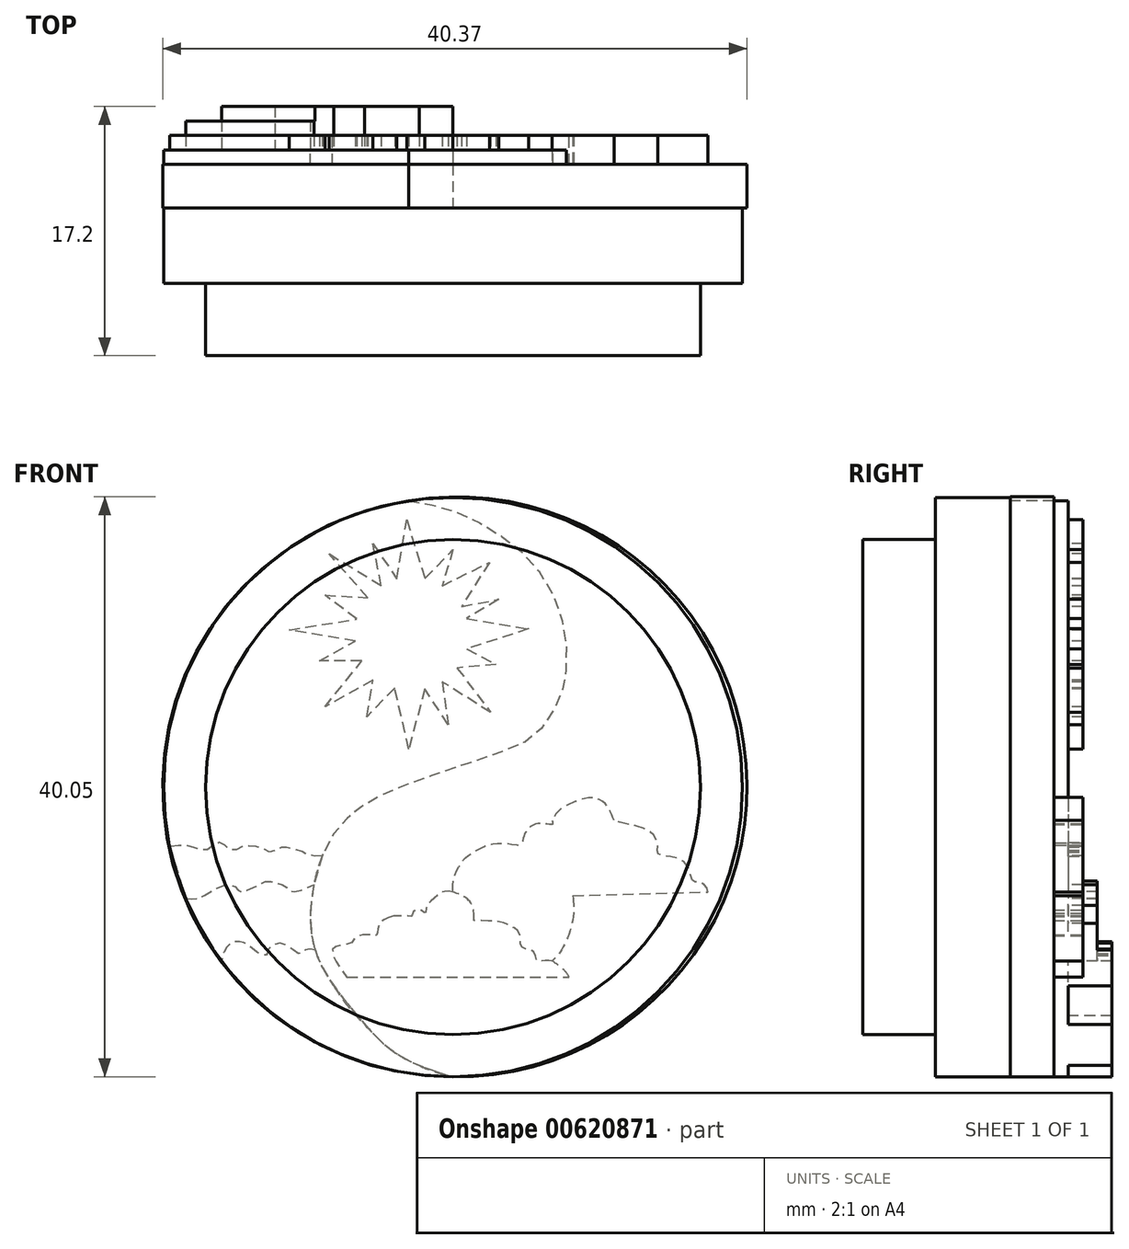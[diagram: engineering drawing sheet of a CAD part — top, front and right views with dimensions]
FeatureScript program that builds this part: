
annotation { "Feature Type Name" : "Feature", "Feature Type Description" : "" }
export const myFeature = defineFeature(function(context is Context, id is Id, definition is map)
    precondition{}
    {
        {
            var Q0;
            Q0=qCreatedBy(makeId("Front.planeOp"),FACE);
            var sketch = newSketch(context, id + "F0", { "sketchPlane" : qUnion([Q0])});
            skCircle(sketch, "E0", {"center": v(0, 0) * mm, "radius": 20 * mm});
            skSolve(sketch);
        }
        {
            var Q0;
            Q0=makeQuery(id+"F0.imprint","IMPRINT",FACE,{"disambiguationData":[TD([[makeQuery(id+"F0.imprint","IMPRINT",EDGE,{"derivedFrom":sQuery(id+"F0.wireOp",EDGE,"E0")}),1.0]])]});
            extrude(context, id + "F1", {"entities" : qUnion([Q0]), "depth" : 5.2 * mm, "offsetDistance" : 25 * mm});
        }
        {
            var Q0;
            Q0=makeQuery(id+"F1.opExtrude","CAP_FACE",FACE,{"disambiguationData":[OSD([sQuery(id+"F0.wireOp",EDGE,"E0")])],"isStart":false});
            var sketch = newSketch(context, id + "F2", { "sketchPlane" : qUnion([Q0])});
            skCircle(sketch, "E1", {"center": v(0, 0) * mm, "radius": 17.1 * mm});
            skSolve(sketch);
        }
        {
            var Q0;
            Q0 = qSketchRegion(id + "F2", true);
            extrude(context, id + "F3", {"entities" : qUnion([Q0]), "operationType" : NewBodyOperationType.ADD, "depth" : 5 * mm, "offsetDistance" : 25 * mm});
        }
        {
            var Q0;
            Q0=makeQuery(id+"F1.opExtrude","CAP_FACE",FACE,{"disambiguationData":[OSD([sQuery(id+"F0.wireOp",EDGE,"E0")])],"isStart":true});
            var sketch = newSketch(context, id + "F4", { "sketchPlane" : qUnion([Q0])});
            skFitSpline(sketch, "E2", {"points": [v(3.07, 19.76) * mm, v(0, 19.09) * mm, v(-3.3, 17.36) * mm, v(-5.79, 15.1) * mm, v(-7.57, 11.43) * mm, v(-7.8, 8.17) * mm, v(-7.39, 6.2) * mm, v(-5.84, 3.77) * mm, v(-3.11, 2.35) * mm, v(3.65, 0) * mm, v(5.9, -1.1) * mm, v(7.45, -2.28) * mm, v(8.87, -4.36) * mm, v(9.7, -7.26) * mm, v(9.76, -10.23) * mm, v(8.81, -12.84) * mm, v(6.8, -15.57) * mm, v(3.89, -18.42) * mm, v(0, -20) * mm], "startDerivative": vector(-55.85, -8.29) * mm, "endDerivative": vector(-65.14, -19.54) * mm});
            skArc(sketch, "E3", {"start": v(3.07, 19.76) * mm, "mid": v(-20.25, 1.56) * mm, "end": v(0, -20) * mm});
            skArc(sketch, "E4", {"start": v(0, -20) * mm, "mid": v(20, -1.54) * mm, "end": v(3.07, 19.76) * mm});
            skFitSpline(sketch, "E5", {"points": [v(9, -4.63) * mm, v(10.3, -4.6) * mm, v(11.5, -4.13) * mm, v(12.14, -4.1) * mm, v(12.34, -4.58) * mm, v(12.1, -5) * mm, v(11.42, -4.83) * mm], "startDerivative": vector(6.16, -0.53) * mm, "endDerivative": vector(-4.8, 2.3) * mm});
            skFitSpline(sketch, "E6", {"points": [v(12.34, -4.5) * mm, v(12.92, -4.39) * mm, v(13.68, -4.12) * mm, v(14.24, -3.86) * mm, v(14.85, -4.03) * mm, v(14.7, -4.75) * mm, v(14.24, -5.02) * mm, v(13.87, -4.83) * mm, v(13.87, -4.58) * mm], "startDerivative": vector(4.3, 0.69) * mm, "endDerivative": vector(0.78, 3.1) * mm});
            skSolve(sketch);
        }
        {
            var Q0;
            {var subQ0=sQuery(id+"F4.wireOp",EDGE,"E2");Q0=makeQuery(id+"F4.imprint","IMPRINT",FACE,{"disambiguationData":[TD([[makeQuery(id+"F4.imprint","IMPRINT",EDGE,{"derivedFrom":subQ0}),1.0]])]});}
            extrude(context, id + "F5", {"entities" : qUnion([Q0]), "operationType" : NewBodyOperationType.ADD, "depth" : 4 * mm, "offsetDistance" : 25 * mm});
        }
        {
            var Q0;
            Q0 = qSketchRegion(id + "F4", true);
            var Q1;
            Q1=makeQuery(id+"F1.opExtrude","CAP_FACE",FACE,{"disambiguationData":[OSD([sQuery(id+"F0.wireOp",EDGE,"E0")])],"isStart":true});
            extrude(context, id + "F6", {"entities" : qUnion([Q0, Q1]), "operationType" : NewBodyOperationType.ADD, "depth" : 3 * mm, "offsetDistance" : 25 * mm});
        }
        {
            var Q0;
            Q0=makeQuery(id+"F5.opExtrude","CAP_FACE",FACE,{"disambiguationData":[OSD([sQuery(id+"F0.wireOp",EDGE,"E0"),sQuery(id+"F4.wireOp",EDGE,"E2")])],"isStart":false});
            var sketch = newSketch(context, id + "F7", { "sketchPlane" : qUnion([Q0])});
            skCircle(sketch, "E7", {"center": v(2.85, 10.6) * mm, "radius": 3.93 * mm});
            skPoint(sketch, "E7.first.point", {"position": v(3.06, 14.51) * mm});
            skPoint(sketch, "E7.second.point", {"position": v(2.98, 6.67) * mm});
            skPoint(sketch, "E7.third.point", {"position": v(4.45, 7) * mm});
            skLineSegment(sketch, "E8", {"start": v(1.94, 6.77) * mm, "end": v(3.06, 2.64) * mm});
            skLineSegment(sketch, "E9", {"start": v(3.06, 2.64) * mm, "end": v(4.03, 6.84) * mm});
            skLineSegment(sketch, "E10", {"start": v(4.03, 6.84) * mm, "end": v(5.96, 4.86) * mm});
            skLineSegment(sketch, "E11", {"start": v(5.96, 4.86) * mm, "end": v(5.54, 7.38) * mm});
            skLineSegment(sketch, "E12", {"start": v(5.54, 7.38) * mm, "end": v(8.85, 5.53) * mm});
            skLineSegment(sketch, "E13", {"start": v(8.85, 5.53) * mm, "end": v(6.3, 8.71) * mm});
            skLineSegment(sketch, "E14", {"start": v(6.3, 8.71) * mm, "end": v(9.23, 8.71) * mm});
            skLineSegment(sketch, "E15", {"start": v(9.23, 8.71) * mm, "end": v(6.75, 10.08) * mm});
            skLineSegment(sketch, "E16", {"start": v(6.75, 10.08) * mm, "end": v(11.33, 10.84) * mm});
            skLineSegment(sketch, "E17", {"start": v(11.33, 10.84) * mm, "end": v(6.65, 11.61) * mm});
            skLineSegment(sketch, "E18", {"start": v(6.65, 11.61) * mm, "end": v(8.85, 13.26) * mm});
            skLineSegment(sketch, "E19", {"start": v(8.85, 13.26) * mm, "end": v(5.9, 13.08) * mm});
            skLineSegment(sketch, "E20", {"start": v(5.9, 13.08) * mm, "end": v(8.56, 16.1) * mm});
            skLineSegment(sketch, "E21", {"start": v(8.56, 16.1) * mm, "end": v(4.95, 13.91) * mm});
            skLineSegment(sketch, "E22", {"start": v(4.95, 13.91) * mm, "end": v(5.54, 16.82) * mm});
            skLineSegment(sketch, "E23", {"start": v(5.54, 16.82) * mm, "end": v(3.88, 14.38) * mm});
            skLineSegment(sketch, "E24", {"start": v(3.88, 14.38) * mm, "end": v(3.2, 18.47) * mm});
            skLineSegment(sketch, "E25", {"start": v(3.2, 18.47) * mm, "end": v(1.95, 14.41) * mm});
            skLineSegment(sketch, "E26", {"start": v(1.95, 14.41) * mm, "end": v(0, 16.4) * mm});
            skLineSegment(sketch, "E27", {"start": v(0, 16.4) * mm, "end": v(0.75, 13.91) * mm});
            skLineSegment(sketch, "E28", {"start": v(0.75, 13.91) * mm, "end": v(-2.52, 15.52) * mm});
            skLineSegment(sketch, "E29", {"start": v(-2.52, 15.52) * mm, "end": v(-0.6, 12.48) * mm});
            skLineSegment(sketch, "E30", {"start": v(-0.6, 12.48) * mm, "end": v(-3.15, 12.96) * mm});
            skLineSegment(sketch, "E31", {"start": v(-3.15, 12.96) * mm, "end": v(-0.93, 11.64) * mm});
            skLineSegment(sketch, "E32", {"start": v(-0.93, 11.64) * mm, "end": v(-5.2, 10.93) * mm});
            skLineSegment(sketch, "E33", {"start": v(-5.2, 10.93) * mm, "end": v(-0.93, 9.54) * mm});
            skLineSegment(sketch, "E34", {"start": v(-0.93, 9.54) * mm, "end": v(-2.98, 8.47) * mm});
            skLineSegment(sketch, "E35", {"start": v(-2.98, 8.47) * mm, "end": v(-0.28, 8.23) * mm});
            skLineSegment(sketch, "E36", {"start": v(-0.28, 8.23) * mm, "end": v(-2.6, 5.16) * mm});
            skLineSegment(sketch, "E37", {"start": v(-2.6, 5.16) * mm, "end": v(0.75, 7.27) * mm});
            skLineSegment(sketch, "E38", {"start": v(0.75, 7.27) * mm, "end": v(0.33, 4.32) * mm});
            skLineSegment(sketch, "E39", {"start": v(0.33, 4.32) * mm, "end": v(1.94, 6.77) * mm});
            skSolve(sketch);
        }
        {
            var Q0;
            {var subQ0=sQuery(id+"F7.wireOp",EDGE,"E7");var subQ8=makeQuery(id+"F7.imprint","INTERSECT",VERTEX,{"derivedFrom":[subQ0,sQuery(id+"F7.wireOp",EDGE,"E17"),sQuery(id+"F7.wireOp",EDGE,"E18")]});Q0=makeQuery(id+"F7.imprint","IMPRINT",FACE,{"disambiguationData":[TD([[makeQuery(id+"F7.imprint","IMPRINT",EDGE,{"disambiguationData":[TD([[subQ8,-1.0]])],"derivedFrom":subQ0}),1.0]])]});}
            var Q1;
            {var subQ0=sQuery(id+"F7.wireOp",EDGE,"E24");Q1=makeQuery(id+"F7.imprint","IMPRINT",FACE,{"disambiguationData":[TD([[makeQuery(id+"F7.imprint","IMPRINT",EDGE,{"derivedFrom":subQ0}),1.0]])]});}
            var Q2;
            {var subQ0=sQuery(id+"F7.wireOp",EDGE,"E22");Q2=makeQuery(id+"F7.imprint","IMPRINT",FACE,{"disambiguationData":[TD([[makeQuery(id+"F7.imprint","IMPRINT",EDGE,{"derivedFrom":subQ0}),1.0]])]});}
            var Q3;
            {var subQ0=sQuery(id+"F7.wireOp",EDGE,"E20");Q3=makeQuery(id+"F7.imprint","IMPRINT",FACE,{"disambiguationData":[TD([[makeQuery(id+"F7.imprint","IMPRINT",EDGE,{"derivedFrom":subQ0}),1.0]])]});}
            var Q4;
            {var subQ0=sQuery(id+"F7.wireOp",EDGE,"E18");Q4=makeQuery(id+"F7.imprint","IMPRINT",FACE,{"disambiguationData":[TD([[makeQuery(id+"F7.imprint","IMPRINT",EDGE,{"derivedFrom":subQ0}),1.0]])]});}
            var Q5;
            {var subQ0=sQuery(id+"F7.wireOp",EDGE,"E16");Q5=makeQuery(id+"F7.imprint","IMPRINT",FACE,{"disambiguationData":[TD([[makeQuery(id+"F7.imprint","IMPRINT",EDGE,{"derivedFrom":subQ0}),1.0]])]});}
            var Q6;
            {var subQ0=sQuery(id+"F7.wireOp",EDGE,"E14");Q6=makeQuery(id+"F7.imprint","IMPRINT",FACE,{"disambiguationData":[TD([[makeQuery(id+"F7.imprint","IMPRINT",EDGE,{"derivedFrom":subQ0}),1.0]])]});}
            var Q7;
            {var subQ0=sQuery(id+"F7.wireOp",EDGE,"E8");Q7=makeQuery(id+"F7.imprint","IMPRINT",FACE,{"disambiguationData":[TD([[makeQuery(id+"F7.imprint","IMPRINT",EDGE,{"derivedFrom":subQ0}),1.0]])]});}
            var Q8;
            {var subQ2=sQuery(id+"F7.wireOp",EDGE,"E38");Q8=makeQuery(id+"F7.imprint","IMPRINT",FACE,{"disambiguationData":[TD([[makeQuery(id+"F7.imprint","IMPRINT",EDGE,{"derivedFrom":subQ2}),1.0]])]});}
            var Q9;
            {var subQ0=sQuery(id+"F7.wireOp",EDGE,"E10");Q9=makeQuery(id+"F7.imprint","IMPRINT",FACE,{"disambiguationData":[TD([[makeQuery(id+"F7.imprint","IMPRINT",EDGE,{"derivedFrom":subQ0}),1.0]])]});}
            var Q10;
            {var subQ0=sQuery(id+"F7.wireOp",EDGE,"E28");Q10=makeQuery(id+"F7.imprint","IMPRINT",FACE,{"disambiguationData":[TD([[makeQuery(id+"F7.imprint","IMPRINT",EDGE,{"derivedFrom":subQ0}),1.0]])]});}
            var Q11;
            {var subQ0=sQuery(id+"F7.wireOp",EDGE,"E36");Q11=makeQuery(id+"F7.imprint","IMPRINT",FACE,{"disambiguationData":[TD([[makeQuery(id+"F7.imprint","IMPRINT",EDGE,{"derivedFrom":subQ0}),1.0]])]});}
            var Q12;
            {var subQ0=sQuery(id+"F7.wireOp",EDGE,"E34");Q12=makeQuery(id+"F7.imprint","IMPRINT",FACE,{"disambiguationData":[TD([[makeQuery(id+"F7.imprint","IMPRINT",EDGE,{"derivedFrom":subQ0}),1.0]])]});}
            var Q13;
            {var subQ0=sQuery(id+"F7.wireOp",EDGE,"E32");Q13=makeQuery(id+"F7.imprint","IMPRINT",FACE,{"disambiguationData":[TD([[makeQuery(id+"F7.imprint","IMPRINT",EDGE,{"derivedFrom":subQ0}),1.0]])]});}
            var Q14;
            {var subQ0=sQuery(id+"F7.wireOp",EDGE,"E30");Q14=makeQuery(id+"F7.imprint","IMPRINT",FACE,{"disambiguationData":[TD([[makeQuery(id+"F7.imprint","IMPRINT",EDGE,{"derivedFrom":subQ0}),1.0]])]});}
            var Q15;
            {var subQ0=sQuery(id+"F7.wireOp",EDGE,"E26");Q15=makeQuery(id+"F7.imprint","IMPRINT",FACE,{"disambiguationData":[TD([[makeQuery(id+"F7.imprint","IMPRINT",EDGE,{"derivedFrom":subQ0}),1.0]])]});}
            extrude(context, id + "F8", {"entities" : qUnion([Q0, Q1, Q2, Q3, Q4, Q5, Q6, Q7, Q8, Q9, Q10, Q11, Q12, Q13, Q14, Q15]), "operationType" : NewBodyOperationType.ADD, "depth" : 1 * mm, "offsetDistance" : 25 * mm});
        }
        {
            var Q0;
            Q0=makeQuery(id+"F5.opExtrude","CAP_FACE",FACE,{"disambiguationData":[OSD([sQuery(id+"F0.wireOp",EDGE,"E0"),sQuery(id+"F4.wireOp",EDGE,"E2")])],"isStart":false});
            var sketch = newSketch(context, id + "F9", { "sketchPlane" : qUnion([Q0])});
            skFitSpline(sketch, "E40", {"points": [v(9.04, -4.74) * mm, v(9.61, -6.74) * mm], "startDerivative": vector(0.57, -2) * mm, "endDerivative": vector(0.57, -2) * mm});
            skFitSpline(sketch, "E41", {"points": [v(9.04, -4.74) * mm, v(9.8, -4.74) * mm, v(10.5, -4.44) * mm, v(11.48, -4.16) * mm, v(11.9, -4.19) * mm, v(12.53, -4.49) * mm, v(13.1, -4.26) * mm, v(14, -4.06) * mm, v(14.6, -4.14) * mm, v(15.25, -4.36) * mm, v(15.82, -3.99) * mm, v(16.27, -3.84) * mm, v(16.97, -4.31) * mm, v(17.5, -4.31) * mm, v(18.39, -4.04) * mm, v(19.57, -4.11) * mm], "startDerivative": vector(11.7, -1.2) * mm, "endDerivative": vector(14.12, -2.18) * mm});
            skFitSpline(sketch, "E42", {"points": [v(19.57, -4.11) * mm, v(18.46, -7.7) * mm], "startDerivative": vector(-1.13, -3.58) * mm, "endDerivative": vector(-1.13, -3.58) * mm});
            skFitSpline(sketch, "E43", {"points": [v(18.46, -7.7) * mm, v(17.7, -7.7) * mm, v(16.67, -7.18) * mm, v(15.82, -6.78) * mm, v(15.12, -6.83) * mm, v(14.8, -7.18) * mm, v(14.42, -7.18) * mm, v(13.52, -6.8) * mm, v(12.8, -6.48) * mm, v(12.2, -6.63) * mm, v(11.53, -6.88) * mm, v(11.3, -7.18) * mm, v(10.55, -7.13) * mm, v(9.61, -6.74) * mm], "startDerivative": vector(-9.4, -1.29) * mm, "endDerivative": vector(-9.93, 4.75) * mm});
            skSolve(sketch);
        }
        {
            var Q0;
            {var subQ0=sQuery(id+"F9.wireOp",EDGE,"E40");Q0=makeQuery(id+"F9.imprint","IMPRINT",FACE,{"disambiguationData":[TD([[makeQuery(id+"F9.imprint","IMPRINT",EDGE,{"derivedFrom":subQ0}),1.0]])]});}
            var Q1;
            {var subQ0=sQuery(id+"F9.wireOp",EDGE,"E41");Q1=makeQuery(id+"F9.imprint","IMPRINT",FACE,{"disambiguationData":[TD([[makeQuery(id+"F9.imprint","IMPRINT",EDGE,{"derivedFrom":subQ0}),-1.0]])]});}
            extrude(context, id + "F10", {"entities" : qUnion([Q0, Q1]), "operationType" : NewBodyOperationType.ADD, "depth" : 1 * mm, "offsetDistance" : 25 * mm});
        }
        {
            var Q0;
            {var subQ0=sQuery(id+"F4.wireOp",EDGE,"E2");var subQ1=sQuery(id+"F0.wireOp",EDGE,"E0");var subQ2=makeQuery(id+"F5.opExtrude","CAP_FACE",FACE,{"disambiguationData":[OSD([subQ1,subQ0])],"isStart":false});var subQ3=sQuery(id+"F9.wireOp",EDGE,"E42");var subQ4=sQuery(id+"F9.wireOp",EDGE,"E40");var subQ5=sQuery(id+"F9.wireOp",EDGE,"E43");Q0=makeQuery(id+"F10.boolean.opBoolean","SPLIT",FACE,{"disambiguationData":[TD([makeQuery(id+"F1.opExtrude","SWEPT_FACE",FACE,{"disambiguationData":[OSD([subQ1])]}),makeQuery(id+"F5.opExtrude","SWEPT_FACE",FACE,{"disambiguationData":[OSD([subQ0])]}),subQ2,makeQuery(id+"F5.opExtrude","SWEPT_FACE",FACE,{"disambiguationData":[OSD([subQ1])]}),makeQuery(id+"F10.opExtrude","SWEPT_FACE",FACE,{"disambiguationData":[OSD([subQ4])]}),makeQuery(id+"F10.opExtrude","CAP_FACE",FACE,{"disambiguationData":[OSD([subQ4,sQuery(id+"F9.wireOp",EDGE,"E41"),subQ3,subQ5])],"isStart":true}),makeQuery(id+"F10.opExtrude","SWEPT_FACE",FACE,{"disambiguationData":[OSD([subQ3])]}),makeQuery(id+"F10.opExtrude","SWEPT_FACE",FACE,{"disambiguationData":[OSD([subQ5])]})])],"derivedFrom":subQ2});}
            var sketch = newSketch(context, id + "F11", { "sketchPlane" : qUnion([Q0])});
            skFitSpline(sketch, "E44", {"points": [v(9.61, -6.74) * mm, v(9.81, -8.17) * mm, v(9.84, -9.4) * mm, v(9.53, -11.24) * mm], "startDerivative": vector(0.66, -4.5) * mm, "endDerivative": vector(-1.08, -5.23) * mm});
            skFitSpline(sketch, "E45", {"points": [v(9.53, -11.24) * mm, v(10.2, -11.24) * mm, v(10.6, -11.5) * mm, v(11.78, -10.8) * mm, v(12.78, -11.24) * mm, v(12.85, -11.58) * mm, v(13.38, -11.5) * mm, v(14.2, -10.86) * mm, v(14.7, -10.68) * mm, v(15.3, -10.76) * mm, v(15.85, -11.45) * mm, v(16, -12.01) * mm], "startDerivative": vector(8.5, 1.66) * mm, "endDerivative": vector(0.84, -6.34) * mm});
            skFitSpline(sketch, "E46", {"points": [v(16, -12.01) * mm, v(17.33, -9.98) * mm, v(18.46, -7.7) * mm], "startDerivative": vector(2.83, 4) * mm, "endDerivative": vector(2.1, 4.62) * mm});
            skSolve(sketch);
        }
        {
            var Q0;
            Q0 = qSketchRegion(id + "F11", true);
            var Q1;
            {var subQ13=sQuery(id+"F11.wireOp",EDGE,"E45");Q1=makeQuery(id+"F11.imprint","IMPRINT",FACE,{"disambiguationData":[TD([[makeQuery(id+"F11.imprint","IMPRINT",EDGE,{"derivedFrom":subQ13}),1.0]])]});}
            extrude(context, id + "F12", {"entities" : qUnion([Q0, Q1]), "operationType" : NewBodyOperationType.ADD, "depth" : 2 * mm, "offsetDistance" : 25 * mm});
        }
        {
            var Q0;
            {var subQ0=sQuery(id+"F11.wireOp",EDGE,"E45");var subQ1=sQuery(id+"F4.wireOp",EDGE,"E2");var subQ2=makeQuery(id+"F5.opExtrude","SWEPT_FACE",FACE,{"disambiguationData":[OSD([subQ1])]});var subQ3=sQuery(id+"F0.wireOp",EDGE,"E0");var subQ4=makeQuery(id+"F5.opExtrude","SWEPT_FACE",FACE,{"disambiguationData":[OSD([subQ3])]});var subQ5=makeQuery(id+"F1.opExtrude","SWEPT_FACE",FACE,{"disambiguationData":[OSD([subQ3])]});var subQ7=makeQuery(id+"F5.opExtrude","CAP_FACE",FACE,{"disambiguationData":[OSD([subQ3,subQ1])],"isStart":false});var subQ8=sQuery(id+"F9.wireOp",EDGE,"E42");var subQ9=makeQuery(id+"F10.opExtrude","SWEPT_FACE",FACE,{"disambiguationData":[OSD([subQ8])]});var subQ10=sQuery(id+"F9.wireOp",EDGE,"E43");var subQ11=makeQuery(id+"F10.opExtrude","SWEPT_FACE",FACE,{"disambiguationData":[OSD([subQ10])]});var subQ15=sQuery(id+"F9.wireOp",EDGE,"E40");var subQ16=makeQuery(id+"F10.opExtrude","SWEPT_FACE",FACE,{"disambiguationData":[OSD([subQ15])]});var subQ17=makeQuery(id+"F10.opExtrude","CAP_FACE",FACE,{"disambiguationData":[OSD([subQ15,sQuery(id+"F9.wireOp",EDGE,"E41"),subQ8,subQ10])],"isStart":true});Q0=makeQuery(id+"F12.boolean.opBoolean","SPLIT",FACE,{"disambiguationData":[TD([makeQuery(id+"F12.opExtrude","SWEPT_FACE",FACE,{"disambiguationData":[OSD([subQ0])]})])],"derivedFrom":makeQuery(id+"F10.boolean.opBoolean","SPLIT",FACE,{"disambiguationData":[TD([subQ5,subQ2,subQ7,subQ4,subQ16,subQ17,subQ9,subQ11])],"derivedFrom":subQ7})});}
            var sketch = newSketch(context, id + "F13", { "sketchPlane" : qUnion([Q0])});
            skFitSpline(sketch, "E47", {"points": [v(9.53, -11.24) * mm, v(8.25, -13.72) * mm, v(6.1, -16.38) * mm, v(2.33, -19.22) * mm, v(0, -20) * mm], "startDerivative": vector(-5.17, -10.88) * mm, "endDerivative": vector(-10.1, -2.38) * mm});
            skFitSpline(sketch, "E48", {"points": [v(0, -20) * mm, v(2.83, -19.8) * mm, v(7.3, -18.62) * mm, v(12.29, -15.78) * mm, v(16, -12.01) * mm], "startDerivative": vector(13.56, 0.53) * mm, "endDerivative": vector(12.82, 14.61) * mm});
            skSolve(sketch);
        }
        {
            var Q0;
            Q0 = qSketchRegion(id + "F13", true);
            var Q1;
            {var subQ9=sQuery(id+"F11.wireOp",EDGE,"E45");var subQ28=makeQuery(id+"F12.opExtrude","CAP_EDGE",EDGE,{"disambiguationData":[OSD([subQ9])],"isStart":true});Q1=makeQuery(id+"F13.imprint","IMPRINT",FACE,{"disambiguationData":[TD([[makeQuery(id+"F13.imprint","IMPRINT",EDGE,{"derivedFrom":subQ28}),-1.0]])]});}
            extrude(context, id + "F14", {"entities" : qUnion([Q0, Q1]), "operationType" : NewBodyOperationType.ADD, "depth" : 3 * mm, "offsetDistance" : 25 * mm});
        }
        {
            var Q0;
            Q0=makeQuery(id+"F6.boolean.opBoolean","SPLIT",FACE,{"disambiguationData":[OD(0.0)],"derivedFrom":makeQuery(id+"F6.opExtrude","CAP_FACE",FACE,{"disambiguationData":[OSD([sQuery(id+"F4.wireOp",EDGE,"E3"),sQuery(id+"F4.wireOp",EDGE,"E4")])],"isStart":false})});
            var sketch = newSketch(context, id + "F15", { "sketchPlane" : qUnion([Q0])});
            skLineSegment(sketch, "E49", {"start": v(-8.28, -7.5) * mm, "end": v(-17.61, -7.23) * mm});
            skFitSpline(sketch, "E50", {"points": [v(-17.61, -7.23) * mm, v(-17.44, -6.81) * mm, v(-16.89, -6.56) * mm, v(-16.56, -6.49) * mm, v(-16.2, -5.41) * mm, v(-15.07, -4.81) * mm, v(-14.14, -4.59) * mm, v(-14.14, -4.12) * mm, v(-13.87, -3.32) * mm, v(-12.97, -2.77) * mm, v(-12, -2.54) * mm, v(-11.12, -2.3) * mm], "startDerivative": vector(1.36, 6.6) * mm, "endDerivative": vector(8.84, 2.8) * mm});
            skFitSpline(sketch, "E51", {"points": [v(-11.12, -2.3) * mm, v(-10.93, -1.8) * mm, v(-10.65, -1.32) * mm, v(-10.08, -0.85) * mm, v(-9.28, -0.75) * mm, v(-8.23, -1.1) * mm, v(-8, -1.2) * mm, v(-7.3, -1.62) * mm, v(-6.86, -2.3) * mm], "startDerivative": vector(1.73, 4.55) * mm, "endDerivative": vector(2.55, -5.25) * mm});
            skFitSpline(sketch, "E52", {"points": [v(-6.86, -2.3) * mm, v(-6.86, -2.57) * mm, v(-6.2, -2.52) * mm, v(-5.51, -2.64) * mm, v(-4.99, -3.14) * mm, v(-4.76, -4.04) * mm], "startDerivative": vector(-0.67, -2.61) * mm, "endDerivative": vector(0.54, -4.01) * mm});
            skFitSpline(sketch, "E53", {"points": [v(-4.76, -4.04) * mm, v(-5.74, -4.36) * mm, v(-6.86, -5.19) * mm, v(-7.8, -6.06) * mm, v(-8.28, -7.5) * mm], "startDerivative": vector(-4.4, -1.02) * mm, "endDerivative": vector(-1.22, -5.87) * mm});
            skFitSpline(sketch, "E54", {"points": [v(-8.28, -7.5) * mm, v(-8.28, -9.09) * mm, v(-7.54, -11.17) * mm, v(-6.86, -12) * mm], "startDerivative": vector(-0.42, -4.45) * mm, "endDerivative": vector(2.52, -2.49) * mm});
            skFitSpline(sketch, "E55", {"points": [v(0, -7.23) * mm, v(0, -6.56) * mm, v(-0.2, -5.9) * mm, v(-0.74, -5) * mm, v(-1.14, -4.67) * mm, v(-2.25, -4.04) * mm, v(-3.39, -3.87) * mm, v(-4.76, -4.04) * mm], "startDerivative": vector(0.3, 5.74) * mm, "endDerivative": vector(-8.15, -1.32) * mm});
            skFitSpline(sketch, "E56", {"points": [v(-6.86, -12) * mm, v(-6.24, -12) * mm, v(-5.82, -12) * mm, v(-5.54, -11.35) * mm, v(-4.75, -11.05) * mm, v(-4.6, -10.15) * mm, v(-3.95, -9.58) * mm, v(-3.34, -9.33) * mm, v(-1.45, -9.2) * mm], "startDerivative": vector(5.77, 0.46) * mm, "endDerivative": vector(11.57, 0.23) * mm});
            skFitSpline(sketch, "E57", {"points": [v(-1.45, -9.2) * mm, v(-1.2, -7.95) * mm, v(0, -7.23) * mm], "startDerivative": vector(0.06, 2.86) * mm, "endDerivative": vector(2.82, 1.1) * mm});
            skFitSpline(sketch, "E58", {"points": [v(-6.86, -12) * mm, v(-8.03, -13.18) * mm], "startDerivative": vector(-1.17, -1.19) * mm, "endDerivative": vector(-1.17, -1.19) * mm});
            skFitSpline(sketch, "E59", {"points": [v(-8.03, -13.18) * mm, v(8.6, -13.18) * mm], "startDerivative": vector(16.63, 0) * mm, "endDerivative": vector(16.63, 0) * mm});
            skFitSpline(sketch, "E60", {"points": [v(9.5, -11.34) * mm, v(8.6, -11.34) * mm, v(7.75, -10.78) * mm, v(7.04, -10.4) * mm, v(6.3, -10.54) * mm, v(5.74, -9.62) * mm, v(4.71, -9.02) * mm, v(3.48, -8.99) * mm, v(2.42, -8.2) * mm, v(1.29, -7.36) * mm, v(0, -7.23) * mm], "startDerivative": vector(-9.99, -1.4) * mm, "endDerivative": vector(-12.26, -0.35) * mm});
            skFitSpline(sketch, "E61", {"points": [v(9.2, -11.39) * mm, v(8.6, -13.18) * mm], "startDerivative": vector(-0.59, -1.8) * mm, "endDerivative": vector(-0.59, -1.8) * mm});
            skSolve(sketch);
        }
        {
            var Q0;
            Q0 = qSketchRegion(id + "F15", true);
            extrude(context, id + "F16", {"entities" : qUnion([Q0]), "operationType" : NewBodyOperationType.ADD, "depth" : 2 * mm, "offsetDistance" : 25 * mm});
        }
        {
            var Q0;
            Q0=makeQuery(id+"F16.opExtrude","CAP_FACE",FACE,{"disambiguationData":[OSD([sQuery(id+"F15.wireOp",EDGE,"E49"),sQuery(id+"F15.wireOp",EDGE,"E50"),sQuery(id+"F15.wireOp",EDGE,"E51"),sQuery(id+"F15.wireOp",EDGE,"E52"),sQuery(id+"F15.wireOp",EDGE,"E54"),sQuery(id+"F15.wireOp",EDGE,"E55"),sQuery(id+"F15.wireOp",EDGE,"E56"),sQuery(id+"F15.wireOp",EDGE,"E57")])],"isStart":false});
            var sketch = newSketch(context, id + "F17", { "sketchPlane" : qUnion([Q0])});
            skFitSpline(sketch, "E62", {"points": [v(0, -7.23) * mm, v(0.7, -7.23) * mm, v(1.28, -7.66) * mm, v(1.81, -8.22) * mm, v(1.92, -8.7) * mm, v(2.2, -8.5) * mm, v(2.4, -8.5) * mm, v(2.54, -8.5) * mm, v(2.73, -8.61) * mm, v(2.85, -8.89) * mm, v(3.2, -8.89) * mm, v(3.57, -8.89) * mm, v(4.19, -8.92) * mm, v(4.21, -8.95) * mm], "startDerivative": vector(6.9, 1.03) * mm, "endDerivative": vector(0.47, -1.2) * mm});
            skFitSpline(sketch, "E63", {"points": [v(4.21, -8.95) * mm, v(4.86, -9.2) * mm, v(5.2, -9.73) * mm, v(5.28, -10.23) * mm, v(5.61, -10.23) * mm, v(6.23, -10.2) * mm, v(6.78, -10.43) * mm, v(7.04, -10.76) * mm, v(8.27, -11.12) * mm, v(7.34, -13.14) * mm], "startDerivative": vector(6.45, -1.82) * mm, "endDerivative": vector(-9.45, -13.1) * mm});
            skFitSpline(sketch, "E64", {"points": [v(7.34, -13.14) * mm, v(-8.02, -13.14) * mm], "startDerivative": vector(-15.37, 0) * mm, "endDerivative": vector(-15.37, 0) * mm});
            skFitSpline(sketch, "E65", {"points": [v(-8.02, -13.14) * mm, v(-7.74, -12.72) * mm, v(-6.86, -12) * mm], "startDerivative": vector(0.55, 1.02) * mm, "endDerivative": vector(1.7, 1.24) * mm});
            skSolve(sketch);
        }
        {
            var Q0;
            Q0=makeQuery(id+"F17.imprint","IMPRINT",FACE,{"disambiguationData":[TD([[makeQuery(id+"F17.imprint","IMPRINT",EDGE,{"derivedFrom":sQuery(id+"F17.wireOp",EDGE,"E62")}),-1.0]])]});
            extrude(context, id + "F18", {"entities" : qUnion([Q0]), "oppositeDirection" : true, "depth" : 2 * mm, "offsetDistance" : 25 * mm});
        }
    });
